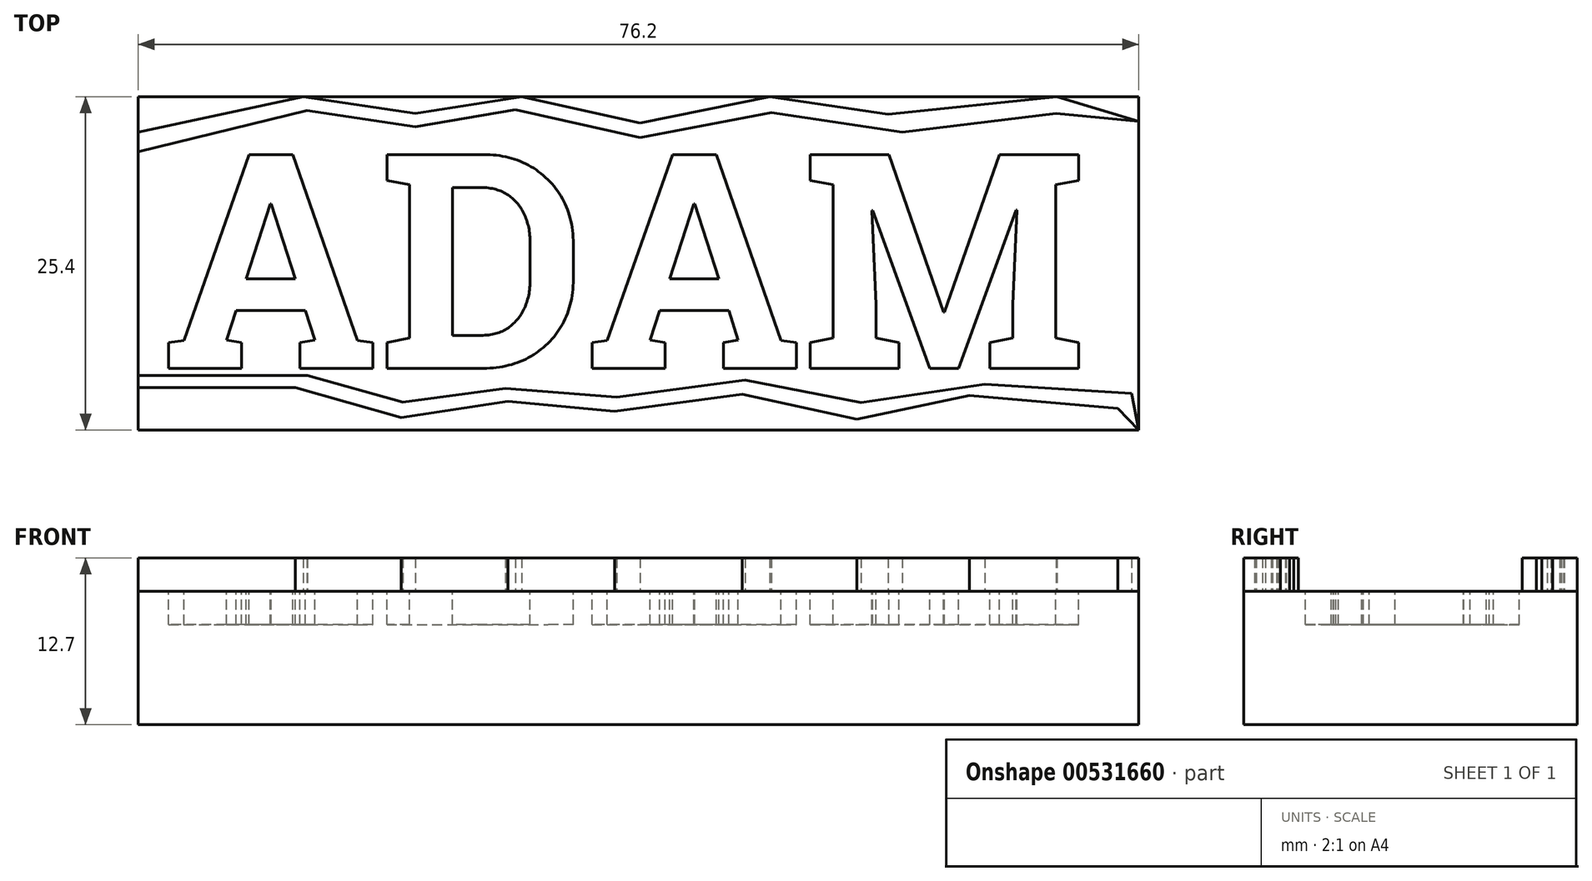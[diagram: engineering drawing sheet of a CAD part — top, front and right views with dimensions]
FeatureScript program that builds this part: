
annotation { "Feature Type Name" : "Feature", "Feature Type Description" : "" }
export const myFeature = defineFeature(function(context is Context, id is Id, definition is map)
    precondition{}
    {
        {
            var Q0;
            Q0=qCreatedBy(makeId("Top.planeOp"),FACE);
            var sketch = newSketch(context, id + "F0", { "sketchPlane" : qUnion([Q0])});
            skLineSegment(sketch, "E0.bottom", {"start": v(-38.2, 11.11) * mm, "end": v(38, 11.11) * mm});
            skLineSegment(sketch, "E0.top", {"start": v(-38.2, -14.29) * mm, "end": v(38, -14.29) * mm});
            skLineSegment(sketch, "E0.left", {"start": v(-38.2, 11.11) * mm, "end": v(-38.2, -14.29) * mm});
            skLineSegment(sketch, "E0.right", {"start": v(38, 11.11) * mm, "end": v(38, -14.29) * mm});
            skSolve(sketch);
        }
        {
            var Q0;
            Q0=makeQuery(id+"F0.imprint","IMPRINT",FACE,{"disambiguationData":[TD([[makeQuery(id+"F0.imprint","IMPRINT",EDGE,{"derivedFrom":sQuery(id+"F0.wireOp",EDGE,"E0.bottom")}),-1.0]])]});
            extrude(context, id + "F1", {"entities" : qUnion([Q0]), "depth" : 10.16 * mm, "offsetDistance" : 25.4 * mm});
        }
        {
            var Q0;
            Q0=makeQuery(id+"F1.opExtrude","CAP_FACE",FACE,{"disambiguationData":[OSD([sQuery(id+"F0.wireOp",EDGE,"E0.bottom"),sQuery(id+"F0.wireOp",EDGE,"E0.top"),sQuery(id+"F0.wireOp",EDGE,"E0.left"),sQuery(id+"F0.wireOp",EDGE,"E0.right")])],"isStart":false});
            var sketch = newSketch(context, id + "F2", { "sketchPlane" : qUnion([Q0])});
            skText(sketch, "E1", { "text": "ADAM", "fontName": "RobotoSlab-Bold.ttf"});
            const initialGuessF2  = {"E1": [-0.03635, -0.00958, 1, 0, 0.0165]};
            skSetInitialGuess(sketch, initialGuessF2);
            skSolve(sketch);
        }
        {
            var Q0;
            Q0 = qSketchRegion(id + "F2", true);
            extrude(context, id + "F3", {"entities" : qUnion([Q0]), "operationType" : NewBodyOperationType.REMOVE, "oppositeDirection" : true, "depth" : 2.54 * mm, "offsetDistance" : 25.4 * mm});
        }
        {
            var Q0;
            {var subQ0=sQuery(id+"F0.wireOp",EDGE,"E0.left");var subQ1=sQuery(id+"F0.wireOp",EDGE,"E0.bottom");var subQ2=sQuery(id+"F0.wireOp",EDGE,"E0.right");var subQ3=sQuery(id+"F0.wireOp",EDGE,"E0.top");Q0=makeQuery(id+"F3.boolean.opBoolean","SPLIT",FACE,{"disambiguationData":[TD([makeQuery(id+"F1.opExtrude","SWEPT_FACE",FACE,{"disambiguationData":[OSD([subQ1])]})])],"derivedFrom":makeQuery(id+"F1.opExtrude","CAP_FACE",FACE,{"disambiguationData":[OSD([subQ1,subQ3,subQ0,subQ2])],"isStart":false})});}
            var sketch = newSketch(context, id + "F4", { "sketchPlane" : qUnion([Q0])});
            skLineSegment(sketch, "E2", {"start": v(-38.2, 8.42) * mm, "end": v(-25.63, 11.11) * mm});
            skLineSegment(sketch, "E3", {"start": v(-25.63, 11.11) * mm, "end": v(-17.11, 9.85) * mm});
            skLineSegment(sketch, "E4", {"start": v(-17.11, 9.85) * mm, "end": v(-9, 11.11) * mm});
            skLineSegment(sketch, "E5", {"start": v(-9, 11.11) * mm, "end": v(0, 9.1) * mm});
            skLineSegment(sketch, "E6", {"start": v(0, 9.1) * mm, "end": v(9.9, 11.11) * mm});
            skLineSegment(sketch, "E7", {"start": v(9.9, 11.11) * mm, "end": v(18.9, 9.78) * mm});
            skLineSegment(sketch, "E8", {"start": v(18.9, 9.78) * mm, "end": v(31.78, 11.11) * mm});
            skLineSegment(sketch, "E9", {"start": v(31.78, 11.11) * mm, "end": v(38, 9.23) * mm});
            skLineSegment(sketch, "E10", {"start": v(38, 9.23) * mm, "end": v(31.71, 9.85) * mm});
            skLineSegment(sketch, "E11", {"start": v(31.71, 9.85) * mm, "end": v(19.98, 8.42) * mm});
            skLineSegment(sketch, "E12", {"start": v(19.98, 8.42) * mm, "end": v(10.02, 9.9) * mm});
            skLineSegment(sketch, "E13", {"start": v(10.02, 9.9) * mm, "end": v(0, 8) * mm});
            skLineSegment(sketch, "E14", {"start": v(0, 8) * mm, "end": v(-9.47, 10.13) * mm});
            skLineSegment(sketch, "E15", {"start": v(-9.47, 10.13) * mm, "end": v(-17.11, 8.82) * mm});
            skLineSegment(sketch, "E16", {"start": v(-17.11, 8.82) * mm, "end": v(-25.36, 10.05) * mm});
            skLineSegment(sketch, "E17", {"start": v(-25.36, 10.05) * mm, "end": v(-38.2, 6.92) * mm});
            skLineSegment(sketch, "E18", {"start": v(-38.2, 6.92) * mm, "end": v(-38.2, 8.42) * mm});
            skSolve(sketch);
        }
        {
            var Q0;
            Q0=makeQuery(id+"F4.imprint","IMPRINT",FACE,{"disambiguationData":[TD([[makeQuery(id+"F4.imprint","IMPRINT",EDGE,{"derivedFrom":sQuery(id+"F4.wireOp",EDGE,"E2")}),-1.0]])]});
            extrude(context, id + "F5", {"entities" : qUnion([Q0]), "operationType" : NewBodyOperationType.ADD, "depth" : 2.54 * mm, "offsetDistance" : 25.4 * mm});
        }
        {
            var Q0;
            {var subQ0=makeQuery(id+"F3.opExtrude","SWEPT_FACE",FACE,{"disambiguationData":[OSD([sQuery(id+"F2.wireOp",EDGE,"E1.sketch_text.stroke-46")])]});var subQ1=makeQuery(id+"F3.opExtrude","SWEPT_FACE",FACE,{"disambiguationData":[OSD([sQuery(id+"F2.wireOp",EDGE,"E1.sketch_text.stroke-41")])]});var subQ2=makeQuery(id+"F3.opExtrude","SWEPT_FACE",FACE,{"disambiguationData":[OSD([sQuery(id+"F2.wireOp",EDGE,"E1.sketch_text.stroke-31"),sQuery(id+"F2.wireOp",EDGE,"E1.sketch_text.stroke-32")])]});var subQ3=makeQuery(id+"F3.opExtrude","SWEPT_FACE",FACE,{"disambiguationData":[OSD([sQuery(id+"F2.wireOp",EDGE,"E1.sketch_text.stroke-30")])]});var subQ4=makeQuery(id+"F3.opExtrude","SWEPT_FACE",FACE,{"disambiguationData":[OSD([sQuery(id+"F2.wireOp",EDGE,"E1.sketch_text.stroke-29")])]});var subQ5=makeQuery(id+"F3.opExtrude","SWEPT_FACE",FACE,{"disambiguationData":[OSD([sQuery(id+"F2.wireOp",EDGE,"E1.sketch_text.stroke-28")])]});var subQ6=makeQuery(id+"F3.opExtrude","SWEPT_FACE",FACE,{"disambiguationData":[OSD([sQuery(id+"F2.wireOp",EDGE,"E1.sketch_text.stroke-27")])]});var subQ7=makeQuery(id+"F3.opExtrude","SWEPT_FACE",FACE,{"disambiguationData":[OSD([sQuery(id+"F2.wireOp",EDGE,"E1.sketch_text.stroke-26")])]});var subQ8=makeQuery(id+"F3.opExtrude","SWEPT_FACE",FACE,{"disambiguationData":[OSD([sQuery(id+"F2.wireOp",EDGE,"E1.sketch_text.stroke-25")])]});var subQ9=makeQuery(id+"F3.opExtrude","SWEPT_FACE",FACE,{"disambiguationData":[OSD([sQuery(id+"F2.wireOp",EDGE,"E1.sketch_text.stroke-24")])]});var subQ10=makeQuery(id+"F3.opExtrude","SWEPT_FACE",FACE,{"disambiguationData":[OSD([sQuery(id+"F2.wireOp",EDGE,"E1.sketch_text.stroke-23")])]});var subQ11=makeQuery(id+"F3.opExtrude","SWEPT_FACE",FACE,{"disambiguationData":[OSD([sQuery(id+"F2.wireOp",EDGE,"E1.sketch_text.stroke-22")])]});var subQ12=makeQuery(id+"F3.opExtrude","SWEPT_FACE",FACE,{"disambiguationData":[OSD([sQuery(id+"F2.wireOp",EDGE,"E1.sketch_text.stroke-51")])]});var subQ13=makeQuery(id+"F3.opExtrude","SWEPT_FACE",FACE,{"disambiguationData":[OSD([sQuery(id+"F2.wireOp",EDGE,"E1.sketch_text.stroke-5")])]});var subQ14=makeQuery(id+"F3.opExtrude","SWEPT_FACE",FACE,{"disambiguationData":[OSD([sQuery(id+"F2.wireOp",EDGE,"E1.sketch_text.stroke-50")])]});var subQ15=makeQuery(id+"F3.opExtrude","SWEPT_FACE",FACE,{"disambiguationData":[OSD([sQuery(id+"F2.wireOp",EDGE,"E1.sketch_text.stroke-4")])]});var subQ16=makeQuery(id+"F3.opExtrude","SWEPT_FACE",FACE,{"disambiguationData":[OSD([sQuery(id+"F2.wireOp",EDGE,"E1.sketch_text.stroke-49")])]});var subQ17=makeQuery(id+"F3.opExtrude","SWEPT_FACE",FACE,{"disambiguationData":[OSD([sQuery(id+"F2.wireOp",EDGE,"E1.sketch_text.stroke-3")])]});var subQ18=makeQuery(id+"F3.opExtrude","SWEPT_FACE",FACE,{"disambiguationData":[OSD([sQuery(id+"F2.wireOp",EDGE,"E1.sketch_text.stroke-48")])]});var subQ19=makeQuery(id+"F3.opExtrude","SWEPT_FACE",FACE,{"disambiguationData":[OSD([sQuery(id+"F2.wireOp",EDGE,"E1.sketch_text.stroke-2")])]});var subQ20=makeQuery(id+"F3.opExtrude","SWEPT_FACE",FACE,{"disambiguationData":[OSD([sQuery(id+"F2.wireOp",EDGE,"E1.sketch_text.stroke-47")])]});var subQ21=makeQuery(id+"F3.opExtrude","SWEPT_FACE",FACE,{"disambiguationData":[OSD([sQuery(id+"F2.wireOp",EDGE,"E1.sketch_text.stroke-1")])]});var subQ22=sQuery(id+"F0.wireOp",EDGE,"E0.right");var subQ23=sQuery(id+"F0.wireOp",EDGE,"E0.left");var subQ24=sQuery(id+"F0.wireOp",EDGE,"E0.top");var subQ25=sQuery(id+"F0.wireOp",EDGE,"E0.bottom");var subQ26=makeQuery(id+"F1.opExtrude","CAP_FACE",FACE,{"disambiguationData":[OSD([subQ25,subQ24,subQ23,subQ22])],"isStart":false});var subQ27=makeQuery(id+"F3.opExtrude","SWEPT_FACE",FACE,{"disambiguationData":[OSD([sQuery(id+"F2.wireOp",EDGE,"E1.sketch_text.stroke-72")])]});var subQ28=makeQuery(id+"F3.opExtrude","SWEPT_FACE",FACE,{"disambiguationData":[OSD([sQuery(id+"F2.wireOp",EDGE,"E1.sketch_text.stroke-11")])]});var subQ29=makeQuery(id+"F3.opExtrude","SWEPT_FACE",FACE,{"disambiguationData":[OSD([sQuery(id+"F2.wireOp",EDGE,"E1.sketch_text.stroke-42")])]});var subQ30=makeQuery(id+"F1.opExtrude","SWEPT_FACE",FACE,{"disambiguationData":[OSD([subQ24])]});var subQ31=makeQuery(id+"F3.opExtrude","SWEPT_FACE",FACE,{"disambiguationData":[OSD([sQuery(id+"F2.wireOp",EDGE,"E1.sketch_text.stroke-73")])]});var subQ32=makeQuery(id+"F3.opExtrude","SWEPT_FACE",FACE,{"disambiguationData":[OSD([sQuery(id+"F2.wireOp",EDGE,"E1.sketch_text.stroke-12")])]});var subQ33=makeQuery(id+"F3.opExtrude","SWEPT_FACE",FACE,{"disambiguationData":[OSD([sQuery(id+"F2.wireOp",EDGE,"E1.sketch_text.stroke-43")])]});var subQ34=makeQuery(id+"F1.opExtrude","SWEPT_FACE",FACE,{"disambiguationData":[OSD([subQ23])]});var subQ35=makeQuery(id+"F3.opExtrude","SWEPT_FACE",FACE,{"disambiguationData":[OSD([sQuery(id+"F2.wireOp",EDGE,"E1.sketch_text.stroke-74")])]});var subQ36=makeQuery(id+"F3.opExtrude","SWEPT_FACE",FACE,{"disambiguationData":[OSD([sQuery(id+"F2.wireOp",EDGE,"E1.sketch_text.stroke-13")])]});var subQ37=makeQuery(id+"F3.opExtrude","SWEPT_FACE",FACE,{"disambiguationData":[OSD([sQuery(id+"F2.wireOp",EDGE,"E1.sketch_text.stroke-45")])]});var subQ38=makeQuery(id+"F3.opExtrude","SWEPT_FACE",FACE,{"disambiguationData":[OSD([sQuery(id+"F2.wireOp",EDGE,"E1.sketch_text.stroke-0")])]});var subQ39=makeQuery(id+"F3.opExtrude","SWEPT_FACE",FACE,{"disambiguationData":[OSD([sQuery(id+"F2.wireOp",EDGE,"E1.sketch_text.stroke-21")])]});var subQ40=makeQuery(id+"F3.opExtrude","SWEPT_FACE",FACE,{"disambiguationData":[OSD([sQuery(id+"F2.wireOp",EDGE,"E1.sketch_text.stroke-44")])]});var subQ41=makeQuery(id+"F1.opExtrude","SWEPT_FACE",FACE,{"disambiguationData":[OSD([subQ22])]});var subQ42=makeQuery(id+"F3.opExtrude","SWEPT_FACE",FACE,{"disambiguationData":[OSD([sQuery(id+"F2.wireOp",EDGE,"E1.sketch_text.stroke-75")])]});var subQ43=makeQuery(id+"F3.opExtrude","SWEPT_FACE",FACE,{"disambiguationData":[OSD([sQuery(id+"F2.wireOp",EDGE,"E1.sketch_text.stroke-14")])]});var subQ44=makeQuery(id+"F3.opExtrude","SWEPT_FACE",FACE,{"disambiguationData":[OSD([sQuery(id+"F2.wireOp",EDGE,"E1.sketch_text.stroke-52")])]});var subQ45=makeQuery(id+"F3.opExtrude","SWEPT_FACE",FACE,{"disambiguationData":[OSD([sQuery(id+"F2.wireOp",EDGE,"E1.sketch_text.stroke-6")])]});var subQ46=makeQuery(id+"F3.opExtrude","SWEPT_FACE",FACE,{"disambiguationData":[OSD([sQuery(id+"F2.wireOp",EDGE,"E1.sketch_text.stroke-53")])]});var subQ47=makeQuery(id+"F3.opExtrude","SWEPT_FACE",FACE,{"disambiguationData":[OSD([sQuery(id+"F2.wireOp",EDGE,"E1.sketch_text.stroke-7")])]});var subQ48=makeQuery(id+"F3.opExtrude","SWEPT_FACE",FACE,{"disambiguationData":[OSD([sQuery(id+"F2.wireOp",EDGE,"E1.sketch_text.stroke-54")])]});var subQ49=makeQuery(id+"F3.opExtrude","SWEPT_FACE",FACE,{"disambiguationData":[OSD([sQuery(id+"F2.wireOp",EDGE,"E1.sketch_text.stroke-8")])]});var subQ50=makeQuery(id+"F3.opExtrude","SWEPT_FACE",FACE,{"disambiguationData":[OSD([sQuery(id+"F2.wireOp",EDGE,"E1.sketch_text.stroke-9")])]});var subQ51=makeQuery(id+"F3.opExtrude","SWEPT_FACE",FACE,{"disambiguationData":[OSD([sQuery(id+"F2.wireOp",EDGE,"E1.sketch_text.stroke-10")])]});var subQ52=makeQuery(id+"F3.opExtrude","SWEPT_FACE",FACE,{"disambiguationData":[OSD([sQuery(id+"F2.wireOp",EDGE,"E1.sketch_text.stroke-15")])]});var subQ53=makeQuery(id+"F3.opExtrude","SWEPT_FACE",FACE,{"disambiguationData":[OSD([sQuery(id+"F2.wireOp",EDGE,"E1.sketch_text.stroke-20")])]});var subQ54=makeQuery(id+"F3.opExtrude","SWEPT_FACE",FACE,{"disambiguationData":[OSD([sQuery(id+"F2.wireOp",EDGE,"E1.sketch_text.stroke-55")])]});var subQ55=makeQuery(id+"F3.opExtrude","SWEPT_FACE",FACE,{"disambiguationData":[OSD([sQuery(id+"F2.wireOp",EDGE,"E1.sketch_text.stroke-56")])]});var subQ56=makeQuery(id+"F3.opExtrude","SWEPT_FACE",FACE,{"disambiguationData":[OSD([sQuery(id+"F2.wireOp",EDGE,"E1.sketch_text.stroke-61")])]});var subQ57=makeQuery(id+"F3.opExtrude","SWEPT_FACE",FACE,{"disambiguationData":[OSD([sQuery(id+"F2.wireOp",EDGE,"E1.sketch_text.stroke-62")])]});var subQ58=makeQuery(id+"F3.opExtrude","SWEPT_FACE",FACE,{"disambiguationData":[OSD([sQuery(id+"F2.wireOp",EDGE,"E1.sketch_text.stroke-63")])]});var subQ59=makeQuery(id+"F3.opExtrude","SWEPT_FACE",FACE,{"disambiguationData":[OSD([sQuery(id+"F2.wireOp",EDGE,"E1.sketch_text.stroke-64")])]});var subQ60=makeQuery(id+"F3.opExtrude","SWEPT_FACE",FACE,{"disambiguationData":[OSD([sQuery(id+"F2.wireOp",EDGE,"E1.sketch_text.stroke-65")])]});var subQ61=makeQuery(id+"F3.opExtrude","SWEPT_FACE",FACE,{"disambiguationData":[OSD([sQuery(id+"F2.wireOp",EDGE,"E1.sketch_text.stroke-66")])]});var subQ62=makeQuery(id+"F3.opExtrude","SWEPT_FACE",FACE,{"disambiguationData":[OSD([sQuery(id+"F2.wireOp",EDGE,"E1.sketch_text.stroke-67")])]});var subQ63=makeQuery(id+"F3.opExtrude","SWEPT_FACE",FACE,{"disambiguationData":[OSD([sQuery(id+"F2.wireOp",EDGE,"E1.sketch_text.stroke-68")])]});var subQ64=makeQuery(id+"F3.opExtrude","SWEPT_FACE",FACE,{"disambiguationData":[OSD([sQuery(id+"F2.wireOp",EDGE,"E1.sketch_text.stroke-69")])]});var subQ65=makeQuery(id+"F3.opExtrude","SWEPT_FACE",FACE,{"disambiguationData":[OSD([sQuery(id+"F2.wireOp",EDGE,"E1.sketch_text.stroke-70")])]});var subQ66=makeQuery(id+"F3.opExtrude","SWEPT_FACE",FACE,{"disambiguationData":[OSD([sQuery(id+"F2.wireOp",EDGE,"E1.sketch_text.stroke-71")])]});var subQ67=makeQuery(id+"F3.opExtrude","SWEPT_FACE",FACE,{"disambiguationData":[OSD([sQuery(id+"F2.wireOp",EDGE,"E1.sketch_text.stroke-76"),sQuery(id+"F2.wireOp",EDGE,"E1.sketch_text.stroke-77")])]});var subQ68=makeQuery(id+"F3.opExtrude","SWEPT_FACE",FACE,{"disambiguationData":[OSD([sQuery(id+"F2.wireOp",EDGE,"E1.sketch_text.stroke-78")])]});var subQ69=makeQuery(id+"F3.opExtrude","SWEPT_FACE",FACE,{"disambiguationData":[OSD([sQuery(id+"F2.wireOp",EDGE,"E1.sketch_text.stroke-79")])]});var subQ70=makeQuery(id+"F3.opExtrude","SWEPT_FACE",FACE,{"disambiguationData":[OSD([sQuery(id+"F2.wireOp",EDGE,"E1.sketch_text.stroke-80")])]});var subQ71=makeQuery(id+"F3.opExtrude","SWEPT_FACE",FACE,{"disambiguationData":[OSD([sQuery(id+"F2.wireOp",EDGE,"E1.sketch_text.stroke-81")])]});var subQ72=makeQuery(id+"F3.opExtrude","SWEPT_FACE",FACE,{"disambiguationData":[OSD([sQuery(id+"F2.wireOp",EDGE,"E1.sketch_text.stroke-82")])]});var subQ73=makeQuery(id+"F3.opExtrude","SWEPT_FACE",FACE,{"disambiguationData":[OSD([sQuery(id+"F2.wireOp",EDGE,"E1.sketch_text.stroke-83")])]});var subQ74=makeQuery(id+"F3.opExtrude","SWEPT_FACE",FACE,{"disambiguationData":[OSD([sQuery(id+"F2.wireOp",EDGE,"E1.sketch_text.stroke-84")])]});var subQ75=makeQuery(id+"F3.opExtrude","SWEPT_FACE",FACE,{"disambiguationData":[OSD([sQuery(id+"F2.wireOp",EDGE,"E1.sketch_text.stroke-85")])]});var subQ76=makeQuery(id+"F3.opExtrude","SWEPT_FACE",FACE,{"disambiguationData":[OSD([sQuery(id+"F2.wireOp",EDGE,"E1.sketch_text.stroke-86")])]});var subQ77=makeQuery(id+"F3.opExtrude","SWEPT_FACE",FACE,{"disambiguationData":[OSD([sQuery(id+"F2.wireOp",EDGE,"E1.sketch_text.stroke-87")])]});var subQ78=makeQuery(id+"F3.opExtrude","SWEPT_FACE",FACE,{"disambiguationData":[OSD([sQuery(id+"F2.wireOp",EDGE,"E1.sketch_text.stroke-88")])]});var subQ79=makeQuery(id+"F3.opExtrude","SWEPT_FACE",FACE,{"disambiguationData":[OSD([sQuery(id+"F2.wireOp",EDGE,"E1.sketch_text.stroke-89")])]});var subQ80=makeQuery(id+"F3.opExtrude","SWEPT_FACE",FACE,{"disambiguationData":[OSD([sQuery(id+"F2.wireOp",EDGE,"E1.sketch_text.stroke-90")])]});var subQ81=makeQuery(id+"F3.opExtrude","SWEPT_FACE",FACE,{"disambiguationData":[OSD([sQuery(id+"F2.wireOp",EDGE,"E1.sketch_text.stroke-91")])]});Q0=makeQuery(id+"F5.boolean.opBoolean","SPLIT",FACE,{"disambiguationData":[TD([subQ26,subQ30,subQ34,subQ41,makeQuery(id+"F3.boolean.opBoolean","COPY",FACE,{"derivedFrom":subQ38}),makeQuery(id+"F3.boolean.opBoolean","COPY",FACE,{"derivedFrom":subQ21}),makeQuery(id+"F3.boolean.opBoolean","COPY",FACE,{"derivedFrom":subQ19}),makeQuery(id+"F3.boolean.opBoolean","COPY",FACE,{"derivedFrom":subQ17}),makeQuery(id+"F3.boolean.opBoolean","COPY",FACE,{"derivedFrom":subQ15}),makeQuery(id+"F3.boolean.opBoolean","COPY",FACE,{"derivedFrom":subQ13}),makeQuery(id+"F3.boolean.opBoolean","COPY",FACE,{"derivedFrom":subQ45}),makeQuery(id+"F3.boolean.opBoolean","COPY",FACE,{"derivedFrom":subQ47}),makeQuery(id+"F3.boolean.opBoolean","COPY",FACE,{"derivedFrom":subQ49}),makeQuery(id+"F3.boolean.opBoolean","COPY",FACE,{"derivedFrom":subQ50}),makeQuery(id+"F3.boolean.opBoolean","COPY",FACE,{"derivedFrom":subQ51}),makeQuery(id+"F3.boolean.opBoolean","COPY",FACE,{"derivedFrom":subQ28}),makeQuery(id+"F3.boolean.opBoolean","COPY",FACE,{"derivedFrom":subQ32}),makeQuery(id+"F3.boolean.opBoolean","COPY",FACE,{"derivedFrom":subQ36}),makeQuery(id+"F3.boolean.opBoolean","COPY",FACE,{"derivedFrom":subQ43}),makeQuery(id+"F3.boolean.opBoolean","COPY",FACE,{"derivedFrom":subQ52}),makeQuery(id+"F3.boolean.opBoolean","COPY",FACE,{"derivedFrom":subQ53}),makeQuery(id+"F3.boolean.opBoolean","COPY",FACE,{"derivedFrom":subQ39}),makeQuery(id+"F3.boolean.opBoolean","COPY",FACE,{"derivedFrom":subQ11}),makeQuery(id+"F3.boolean.opBoolean","COPY",FACE,{"derivedFrom":subQ10}),makeQuery(id+"F3.boolean.opBoolean","COPY",FACE,{"derivedFrom":subQ9}),makeQuery(id+"F3.boolean.opBoolean","COPY",FACE,{"derivedFrom":subQ8}),makeQuery(id+"F3.boolean.opBoolean","COPY",FACE,{"derivedFrom":subQ7}),makeQuery(id+"F3.boolean.opBoolean","COPY",FACE,{"derivedFrom":subQ6}),makeQuery(id+"F3.boolean.opBoolean","COPY",FACE,{"derivedFrom":subQ5}),makeQuery(id+"F3.boolean.opBoolean","COPY",FACE,{"derivedFrom":subQ4}),makeQuery(id+"F3.boolean.opBoolean","COPY",FACE,{"derivedFrom":subQ3}),makeQuery(id+"F3.boolean.opBoolean","COPY",FACE,{"derivedFrom":subQ2}),makeQuery(id+"F3.boolean.opBoolean","COPY",FACE,{"derivedFrom":subQ1}),makeQuery(id+"F3.boolean.opBoolean","COPY",FACE,{"derivedFrom":subQ29}),makeQuery(id+"F3.boolean.opBoolean","COPY",FACE,{"derivedFrom":subQ33}),makeQuery(id+"F3.boolean.opBoolean","COPY",FACE,{"derivedFrom":subQ40}),makeQuery(id+"F3.boolean.opBoolean","COPY",FACE,{"derivedFrom":subQ37}),makeQuery(id+"F3.boolean.opBoolean","COPY",FACE,{"derivedFrom":subQ0}),makeQuery(id+"F3.boolean.opBoolean","COPY",FACE,{"derivedFrom":subQ20}),makeQuery(id+"F3.boolean.opBoolean","COPY",FACE,{"derivedFrom":subQ18}),makeQuery(id+"F3.boolean.opBoolean","COPY",FACE,{"derivedFrom":subQ16}),makeQuery(id+"F3.boolean.opBoolean","COPY",FACE,{"derivedFrom":subQ14}),makeQuery(id+"F3.boolean.opBoolean","COPY",FACE,{"derivedFrom":subQ12}),makeQuery(id+"F3.boolean.opBoolean","COPY",FACE,{"derivedFrom":subQ44}),makeQuery(id+"F3.boolean.opBoolean","COPY",FACE,{"derivedFrom":subQ46}),makeQuery(id+"F3.boolean.opBoolean","COPY",FACE,{"derivedFrom":subQ48}),makeQuery(id+"F3.boolean.opBoolean","COPY",FACE,{"derivedFrom":subQ54}),makeQuery(id+"F3.boolean.opBoolean","COPY",FACE,{"derivedFrom":subQ55}),makeQuery(id+"F3.boolean.opBoolean","COPY",FACE,{"derivedFrom":subQ56}),makeQuery(id+"F3.boolean.opBoolean","COPY",FACE,{"derivedFrom":subQ57}),makeQuery(id+"F3.boolean.opBoolean","COPY",FACE,{"derivedFrom":subQ58}),makeQuery(id+"F3.boolean.opBoolean","COPY",FACE,{"derivedFrom":subQ59}),makeQuery(id+"F3.boolean.opBoolean","COPY",FACE,{"derivedFrom":subQ60}),makeQuery(id+"F3.boolean.opBoolean","COPY",FACE,{"derivedFrom":subQ61}),makeQuery(id+"F3.boolean.opBoolean","COPY",FACE,{"derivedFrom":subQ62}),makeQuery(id+"F3.boolean.opBoolean","COPY",FACE,{"derivedFrom":subQ63}),makeQuery(id+"F3.boolean.opBoolean","COPY",FACE,{"derivedFrom":subQ64}),makeQuery(id+"F3.boolean.opBoolean","COPY",FACE,{"derivedFrom":subQ65}),makeQuery(id+"F3.boolean.opBoolean","COPY",FACE,{"derivedFrom":subQ66}),makeQuery(id+"F3.boolean.opBoolean","COPY",FACE,{"derivedFrom":subQ27}),makeQuery(id+"F3.boolean.opBoolean","COPY",FACE,{"derivedFrom":subQ31}),makeQuery(id+"F3.boolean.opBoolean","COPY",FACE,{"derivedFrom":subQ35}),makeQuery(id+"F3.boolean.opBoolean","COPY",FACE,{"derivedFrom":subQ42}),makeQuery(id+"F3.boolean.opBoolean","COPY",FACE,{"derivedFrom":subQ67}),makeQuery(id+"F3.boolean.opBoolean","COPY",FACE,{"derivedFrom":subQ68}),makeQuery(id+"F3.boolean.opBoolean","COPY",FACE,{"derivedFrom":subQ69}),makeQuery(id+"F3.boolean.opBoolean","COPY",FACE,{"derivedFrom":subQ70}),makeQuery(id+"F3.boolean.opBoolean","COPY",FACE,{"derivedFrom":subQ71}),makeQuery(id+"F3.boolean.opBoolean","COPY",FACE,{"derivedFrom":subQ72}),makeQuery(id+"F3.boolean.opBoolean","COPY",FACE,{"derivedFrom":subQ73}),makeQuery(id+"F3.boolean.opBoolean","COPY",FACE,{"derivedFrom":subQ74}),makeQuery(id+"F3.boolean.opBoolean","COPY",FACE,{"derivedFrom":subQ75}),makeQuery(id+"F3.boolean.opBoolean","COPY",FACE,{"derivedFrom":subQ76}),makeQuery(id+"F3.boolean.opBoolean","COPY",FACE,{"derivedFrom":subQ77}),makeQuery(id+"F3.boolean.opBoolean","COPY",FACE,{"derivedFrom":subQ78}),makeQuery(id+"F3.boolean.opBoolean","COPY",FACE,{"derivedFrom":subQ79}),makeQuery(id+"F3.boolean.opBoolean","COPY",FACE,{"derivedFrom":subQ80}),makeQuery(id+"F3.boolean.opBoolean","COPY",FACE,{"derivedFrom":subQ81}),makeQuery(id+"F5.opExtrude","SWEPT_FACE",FACE,{"disambiguationData":[OSD([sQuery(id+"F4.wireOp",EDGE,"E9")])]}),makeQuery(id+"F5.opExtrude","SWEPT_FACE",FACE,{"disambiguationData":[OSD([sQuery(id+"F4.wireOp",EDGE,"E10")])]}),makeQuery(id+"F5.opExtrude","SWEPT_FACE",FACE,{"disambiguationData":[OSD([sQuery(id+"F4.wireOp",EDGE,"E11")])]}),makeQuery(id+"F5.opExtrude","SWEPT_FACE",FACE,{"disambiguationData":[OSD([sQuery(id+"F4.wireOp",EDGE,"E12")])]}),makeQuery(id+"F5.opExtrude","SWEPT_FACE",FACE,{"disambiguationData":[OSD([sQuery(id+"F4.wireOp",EDGE,"E13")])]}),makeQuery(id+"F5.opExtrude","SWEPT_FACE",FACE,{"disambiguationData":[OSD([sQuery(id+"F4.wireOp",EDGE,"E14")])]}),makeQuery(id+"F5.opExtrude","SWEPT_FACE",FACE,{"disambiguationData":[OSD([sQuery(id+"F4.wireOp",EDGE,"E15")])]}),makeQuery(id+"F5.opExtrude","SWEPT_FACE",FACE,{"disambiguationData":[OSD([sQuery(id+"F4.wireOp",EDGE,"E16")])]}),makeQuery(id+"F5.opExtrude","SWEPT_FACE",FACE,{"disambiguationData":[OSD([sQuery(id+"F4.wireOp",EDGE,"E17")])]}),makeQuery(id+"F5.opExtrude","SWEPT_FACE",FACE,{"disambiguationData":[OSD([sQuery(id+"F4.wireOp",EDGE,"E18")])]})])],"derivedFrom":makeQuery(id+"F3.boolean.opBoolean","SPLIT",FACE,{"disambiguationData":[TD([makeQuery(id+"F1.opExtrude","SWEPT_FACE",FACE,{"disambiguationData":[OSD([subQ25])]})])],"derivedFrom":subQ26})});}
            var sketch = newSketch(context, id + "F6", { "sketchPlane" : qUnion([Q0])});
            skLineSegment(sketch, "E19", {"start": v(-38.2, -11.07) * mm, "end": v(-26.23, -11.07) * mm});
            skLineSegment(sketch, "E20", {"start": v(-26.23, -11.07) * mm, "end": v(-18.19, -13.33) * mm});
            skLineSegment(sketch, "E21", {"start": v(-18.19, -13.33) * mm, "end": v(-10.06, -12.1) * mm});
            skLineSegment(sketch, "E22", {"start": v(-10.06, -12.1) * mm, "end": v(-1.91, -12.85) * mm});
            skLineSegment(sketch, "E23", {"start": v(-1.91, -12.85) * mm, "end": v(7.8, -11.55) * mm});
            skLineSegment(sketch, "E24", {"start": v(7.8, -11.55) * mm, "end": v(16.52, -13.46) * mm});
            skLineSegment(sketch, "E25", {"start": v(16.52, -13.46) * mm, "end": v(25.11, -11.65) * mm});
            skLineSegment(sketch, "E26", {"start": v(25.11, -11.65) * mm, "end": v(36.39, -12.62) * mm});
            skLineSegment(sketch, "E27", {"start": v(36.39, -12.62) * mm, "end": v(38, -14.29) * mm});
            skLineSegment(sketch, "E28", {"start": v(38, -14.29) * mm, "end": v(37.45, -11.5) * mm});
            skLineSegment(sketch, "E29", {"start": v(37.45, -11.5) * mm, "end": v(26.28, -10.8) * mm});
            skLineSegment(sketch, "E30", {"start": v(26.28, -10.8) * mm, "end": v(16.84, -12.19) * mm});
            skLineSegment(sketch, "E31", {"start": v(16.84, -12.19) * mm, "end": v(8.03, -10.48) * mm});
            skLineSegment(sketch, "E32", {"start": v(8.03, -10.48) * mm, "end": v(-1.77, -11.79) * mm});
            skLineSegment(sketch, "E33", {"start": v(-1.77, -11.79) * mm, "end": v(-10.24, -11.12) * mm});
            skLineSegment(sketch, "E34", {"start": v(-10.24, -11.12) * mm, "end": v(-18.05, -12.16) * mm});
            skLineSegment(sketch, "E35", {"start": v(-18.05, -12.16) * mm, "end": v(-25.31, -10.12) * mm});
            skLineSegment(sketch, "E36", {"start": v(-25.31, -10.12) * mm, "end": v(-38.2, -10.12) * mm});
            skLineSegment(sketch, "E37", {"start": v(-38.2, -10.12) * mm, "end": v(-38.2, -11.07) * mm});
            skSolve(sketch);
        }
        {
            var Q0;
            Q0=makeQuery(id+"F6.imprint","IMPRINT",FACE,{"disambiguationData":[TD([[makeQuery(id+"F6.imprint","IMPRINT",EDGE,{"derivedFrom":sQuery(id+"F6.wireOp",EDGE,"E19")}),1.0]])]});
            extrude(context, id + "F7", {"entities" : qUnion([Q0]), "operationType" : NewBodyOperationType.ADD, "depth" : 2.54 * mm, "offsetDistance" : 25.4 * mm});
        }
    });
